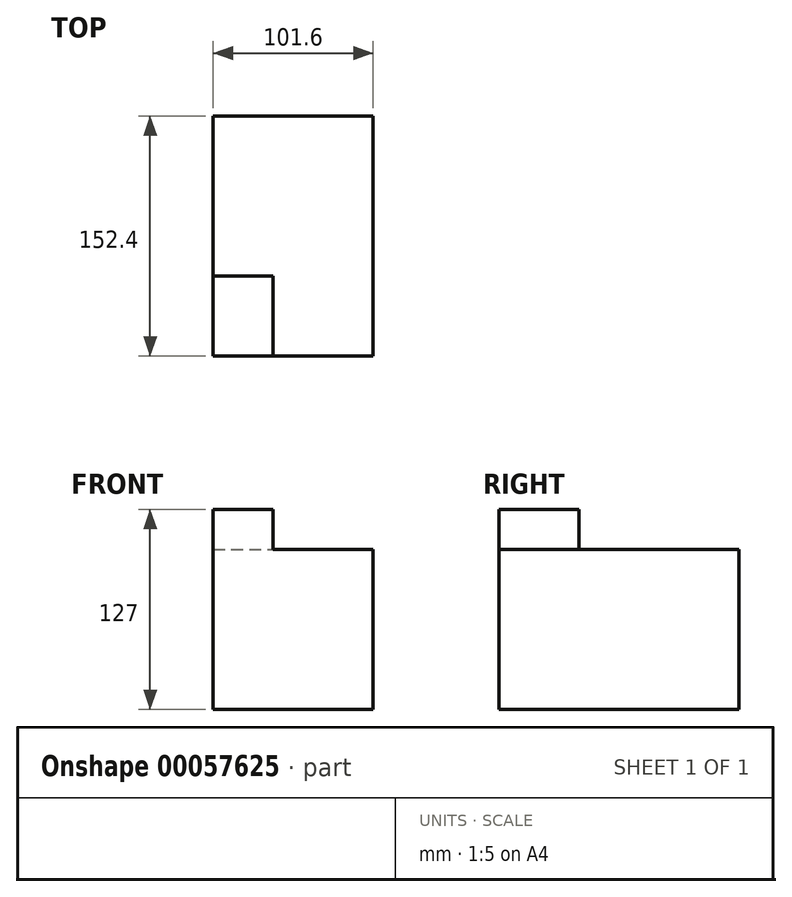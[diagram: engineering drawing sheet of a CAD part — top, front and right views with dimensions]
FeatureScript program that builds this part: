
annotation { "Feature Type Name" : "Feature", "Feature Type Description" : "" }
export const myFeature = defineFeature(function(context is Context, id is Id, definition is map)
    precondition{}
    {
        {
            var Q0;
            Q0=qCreatedBy(makeId("Top.planeOp"),FACE);
            var sketch = newSketch(context, id + "F0", { "sketchPlane" : qUnion([Q0])});
            skLineSegment(sketch, "E0.rect.bottom", {"start": v(50.8, -76.2) * mm, "end": v(-50.8, -76.2) * mm});
            skLineSegment(sketch, "E0.rect.top", {"start": v(50.8, 76.2) * mm, "end": v(-50.8, 76.2) * mm});
            skLineSegment(sketch, "E0.rect.left", {"start": v(50.8, -76.2) * mm, "end": v(50.8, 76.2) * mm});
            skLineSegment(sketch, "E0.rect.right", {"start": v(-50.8, -76.2) * mm, "end": v(-50.8, 76.2) * mm});
            skPoint(sketch, "E0.rect.middle", {"position": v(0, 0) * mm});
            skSolve(sketch);
        }
        {
            var Q0;
            Q0 = qSketchRegion(id + "F0", true);
            extrude(context, id + "F1", {"entities" : qUnion([Q0]), "endBound" : BoundingType.SYMMETRIC, "depth" : 101.6 * mm});
        }
        {
            var Q0;
            Q0=makeQuery(id+"F1.opExtrude","CAP_FACE",FACE,{"disambiguationData":[OSD([sQuery(id+"F0.wireOp",EDGE,"E0.rect.bottom"),sQuery(id+"F0.wireOp",EDGE,"E0.rect.top"),sQuery(id+"F0.wireOp",EDGE,"E0.rect.left"),sQuery(id+"F0.wireOp",EDGE,"E0.rect.right")])],"isStart":false});
            var sketch = newSketch(context, id + "F2", { "sketchPlane" : qUnion([Q0])});
            skLineSegment(sketch, "E1.bottom", {"start": v(-50.8, -76.2) * mm, "end": v(-12.7, -76.2) * mm});
            skLineSegment(sketch, "E1.top", {"start": v(-50.8, -25.4) * mm, "end": v(-12.7, -25.4) * mm});
            skLineSegment(sketch, "E1.left", {"start": v(-50.8, -76.2) * mm, "end": v(-50.8, -25.4) * mm});
            skLineSegment(sketch, "E1.right", {"start": v(-12.7, -76.2) * mm, "end": v(-12.7, -25.4) * mm});
            skSolve(sketch);
        }
        {
            var Q0;
            Q0=makeQuery(id+"F2.imprint","IMPRINT",FACE,{"disambiguationData":[TD([[makeQuery(id+"F2.imprint","IMPRINT",EDGE,{"derivedFrom":sQuery(id+"F2.wireOp",EDGE,"E1.bottom")}),-1.0]])]});
            extrude(context, id + "F3", {"entities" : qUnion([Q0]), "operationType" : NewBodyOperationType.ADD, "depth" : 25.4 * mm});
        }
    });
